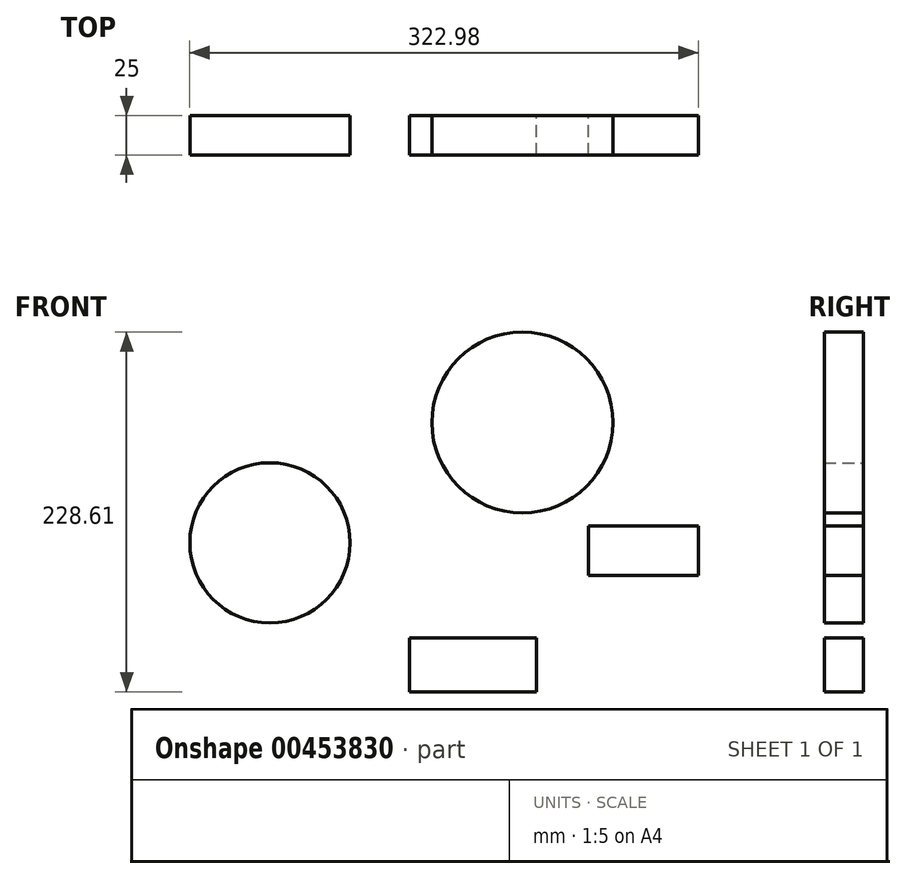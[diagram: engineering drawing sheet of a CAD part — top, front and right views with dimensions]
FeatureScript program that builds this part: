
annotation { "Feature Type Name" : "Feature", "Feature Type Description" : "" }
export const myFeature = defineFeature(function(context is Context, id is Id, definition is map)
    precondition{}
    {
        {
            var Q0;
            Q0=qCreatedBy(makeId("Front.planeOp"),FACE);
            var sketch = newSketch(context, id + "F0", { "sketchPlane" : qUnion([Q0])});
            skCircle(sketch, "E0", {"center": v(-169.17, 0) * mm, "radius": 50.87 * mm});
            skCircle(sketch, "E1", {"center": v(-8.8, 76.42) * mm, "radius": 57.49 * mm});
            skSolve(sketch);
        }
        {
            var Q0;
            Q0=qCreatedBy(makeId("Front.planeOp"),FACE);
            var sketch = newSketch(context, id + "F1", { "sketchPlane" : qUnion([Q0])});
            skLineSegment(sketch, "E2.bottom", {"start": v(-80.55, -60.37) * mm, "end": v(0, -60.37) * mm});
            skLineSegment(sketch, "E2.top", {"start": v(-80.55, -94.7) * mm, "end": v(0, -94.7) * mm});
            skLineSegment(sketch, "E2.left", {"start": v(-80.55, -60.37) * mm, "end": v(-80.55, -94.7) * mm});
            skLineSegment(sketch, "E2.right", {"start": v(0, -60.37) * mm, "end": v(0, -94.7) * mm});
            skSolve(sketch);
        }
        {
            var Q0;
            Q0=qCreatedBy(makeId("Front.planeOp"),FACE);
            var sketch = newSketch(context, id + "F2", { "sketchPlane" : qUnion([Q0])});
            skLineSegment(sketch, "E3.bottom", {"start": v(33.3, 10.89) * mm, "end": v(102.94, 10.89) * mm});
            skLineSegment(sketch, "E3.top", {"start": v(33.3, -20.8) * mm, "end": v(102.94, -20.8) * mm});
            skLineSegment(sketch, "E3.left", {"start": v(33.3, 10.89) * mm, "end": v(33.3, -20.8) * mm});
            skLineSegment(sketch, "E3.right", {"start": v(102.94, 10.89) * mm, "end": v(102.94, -20.8) * mm});
            skSolve(sketch);
        }
        {
            var Q0;
            Q0=makeQuery(id+"F0.imprint","IMPRINT",FACE,{"disambiguationData":[TD([[makeQuery(id+"F0.imprint","IMPRINT",EDGE,{"derivedFrom":sQuery(id+"F0.wireOp",EDGE,"E0")}),1.0]])]});
            var Q1;
            Q1=makeQuery(id+"F0.imprint","IMPRINT",FACE,{"disambiguationData":[TD([[makeQuery(id+"F0.imprint","IMPRINT",EDGE,{"derivedFrom":sQuery(id+"F0.wireOp",EDGE,"E1")}),1.0]])]});
            var Q2;
            Q2=makeQuery(id+"F2.imprint","IMPRINT",FACE,{"disambiguationData":[TD([[makeQuery(id+"F2.imprint","IMPRINT",EDGE,{"derivedFrom":sQuery(id+"F2.wireOp",EDGE,"E3.bottom")}),-1.0]])]});
            var Q3;
            Q3=makeQuery(id+"F1.imprint","IMPRINT",FACE,{"disambiguationData":[TD([[makeQuery(id+"F1.imprint","IMPRINT",EDGE,{"derivedFrom":sQuery(id+"F1.wireOp",EDGE,"E2.bottom")}),-1.0]])]});
            extrude(context, id + "F3", {"entities" : qUnion([Q0, Q1, Q2, Q3]), "depth" : 25 * mm});
        }
    });
